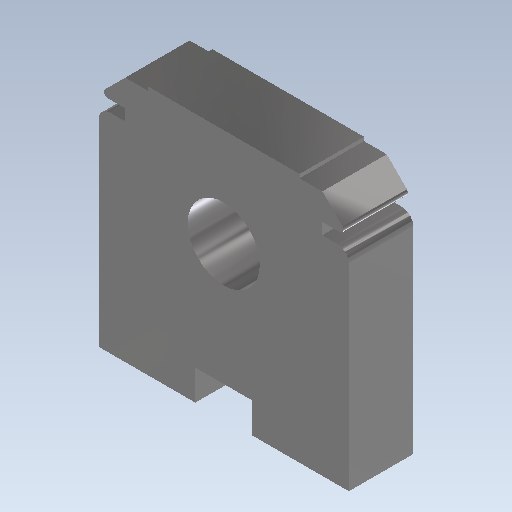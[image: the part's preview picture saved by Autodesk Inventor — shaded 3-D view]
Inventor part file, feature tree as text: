
AUTODESK INVENTOR PART (.ipt)
format: ipt  version: 2021.3 (Build 253353000, 353)  size: 180,736 bytes
history: native  units: mm
features: extrude x5, sketch x5, fillet x2, chamfer x1
ambient origin geometry x8: Origin, YZ Plane, XZ Plane, XY Plane, X Axis, Y Axis, Z Axis, Center Point
bodies: Solid1 (feature_tree)
feature tree (13):
  extrude  "Extrusion1"  Depth=66.0mm
  extrude  "Extrusion2"  Depth=40.0mm
  chamfer  "Chamfer1"  Distance=17.0mm
  extrude  "Extrusion3"  Depth=7.0mm
  fillet  "Fillet1"  Radius=3.0mm
  fillet  "Fillet2"  Radius=7.0mm
  extrude  "Extrusion4"  Depth=17.0mm TaperAngle=0.0deg
  extrude  "Extrusion5"  Depth=1.0mm
  sketch  "Sketch2"  dims[d17=66.0mm d18=66.0mm]
  sketch  "Sketch3"  dims[d19=17.0mm d20=0.0mm d21=40.0mm]
  sketch  "Sketch4"  dims[d22=1.0mm d23=17.0mm d24=0.0mm]
  sketch  "Sketch5"  dims[d25=7.0mm d26=2.0mm d27=45.0deg d28=7.0mm d29=3.0mm d30=7.0mm]
  sketch  "Sketch6"  dims[d31=3.0mm d32=17.0mm d33=0.0mm d34=1.0mm d35=3.0mm d36=15.0mm d37=8.0mm d38=17.0mm d39=0.0mm d40=19.0mm d41=26.0mm d42=33.0mm d43=17.0mm d44=0.0mm]
